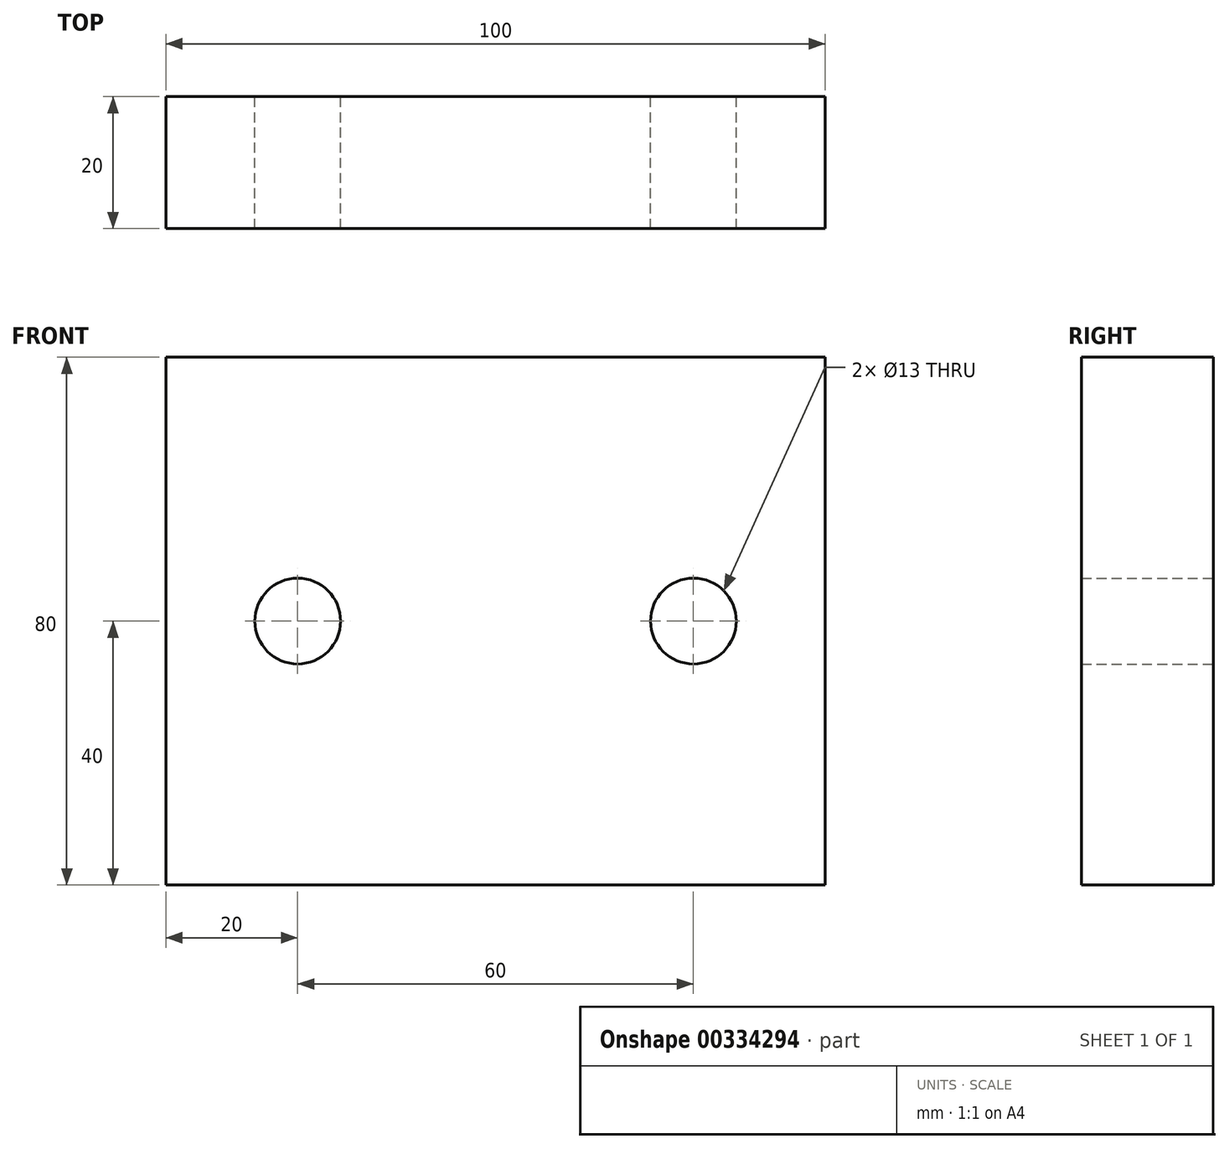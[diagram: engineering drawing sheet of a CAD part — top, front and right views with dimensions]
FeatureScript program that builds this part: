
annotation { "Feature Type Name" : "Feature", "Feature Type Description" : "" }
export const myFeature = defineFeature(function(context is Context, id is Id, definition is map)
    precondition{}
    {
        {
            var Q0;
            Q0=qCreatedBy(makeId("Front.planeOp"),FACE);
            var sketch = newSketch(context, id + "F0", { "sketchPlane" : qUnion([Q0])});
            skLineSegment(sketch, "E0.bottom", {"start": v(50, 40) * mm, "end": v(-50, 40) * mm});
            skLineSegment(sketch, "E0.top", {"start": v(50, -40) * mm, "end": v(-50, -40) * mm});
            skLineSegment(sketch, "E0.left", {"start": v(50, 40) * mm, "end": v(50, -40) * mm});
            skLineSegment(sketch, "E0.right", {"start": v(-50, 40) * mm, "end": v(-50, -40) * mm});
            skPoint(sketch, "E0.middle", {"position": v(0, 0) * mm});
            skLineSegment(sketch, "E1", {"start": v(-50, 0) * mm, "end": v(50, 0) * mm, "construction": true});
            skLineSegment(sketch, "E2", {"start": v(0, 40) * mm, "end": v(0, -40) * mm, "construction": true});
            skCircle(sketch, "E3", {"center": v(-30, 0) * mm, "radius": 6.5 * mm});
            skCircle(sketch, "E4", {"center": v(30, 0) * mm, "radius": 6.5 * mm});
            skSolve(sketch);
        }
        {
            var Q0;
            Q0=makeQuery(id+"F0.imprint","IMPRINT",FACE,{"disambiguationData":[TD([[makeQuery(id+"F0.imprint","IMPRINT",EDGE,{"derivedFrom":sQuery(id+"F0.wireOp",EDGE,"E0.bottom")}),1.0]])]});
            extrude(context, id + "F1", {"entities" : qUnion([Q0]), "depth" : 20 * mm});
        }
    });
